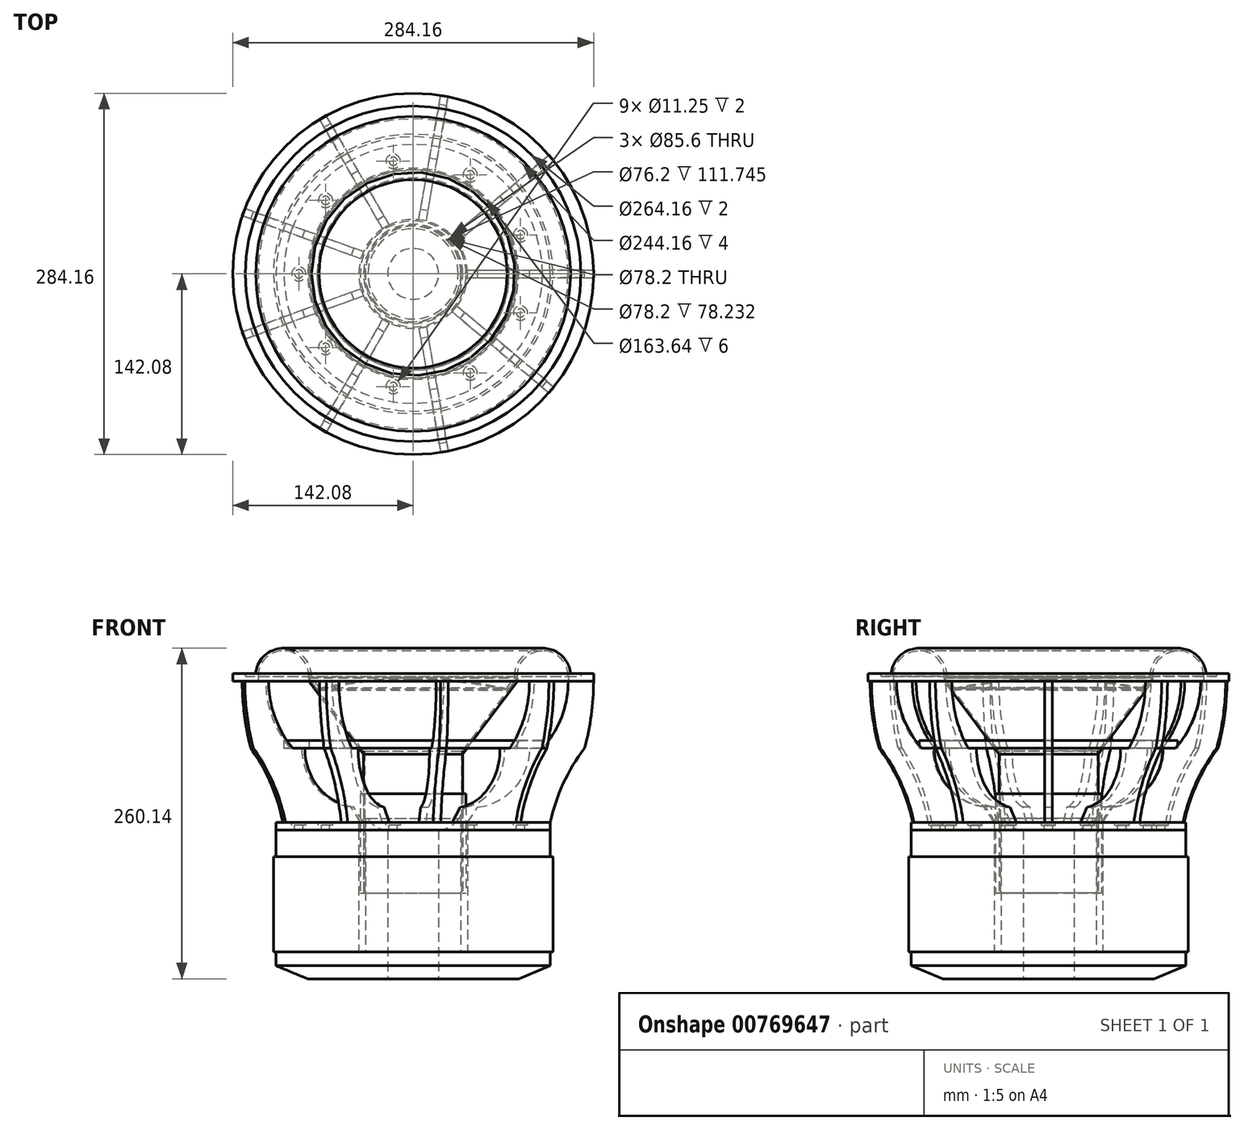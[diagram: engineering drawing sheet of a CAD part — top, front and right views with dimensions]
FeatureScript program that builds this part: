
annotation { "Feature Type Name" : "Feature", "Feature Type Description" : "" }
export const myFeature = defineFeature(function(context is Context, id is Id, definition is map)
    precondition{}
    {
        {
            var Q0;
            Q0=qCreatedBy(makeId("Front.planeOp"),FACE);
            var sketch = newSketch(context, id + "F0", { "sketchPlane" : qUnion([Q0])});
            skLineSegment(sketch, "E0.bottom", {"start": v(42.8, 0) * mm, "end": v(108, 0) * mm});
            skLineSegment(sketch, "E0.top", {"start": v(42.8, -6) * mm, "end": v(108, -6) * mm});
            skLineSegment(sketch, "E0.left", {"start": v(42.8, 0) * mm, "end": v(42.8, -6) * mm});
            skLineSegment(sketch, "E1", {"start": v(108, -6) * mm, "end": v(108, 0) * mm});
            skLineSegment(sketch, "E2", {"start": v(0, 0) * mm, "end": v(0, 32.36) * mm, "construction": true});
            skLineSegment(sketch, "E3.bottom", {"start": v(132.08, 117.12) * mm, "end": v(142.08, 117.12) * mm});
            skLineSegment(sketch, "E3.top", {"start": v(122.08, 111.12) * mm, "end": v(142.08, 111.12) * mm});
            skLineSegment(sketch, "E3.left", {"start": v(122.08, 115.12) * mm, "end": v(122.08, 111.12) * mm});
            skLineSegment(sketch, "E3.right", {"start": v(142.08, 117.12) * mm, "end": v(142.08, 111.12) * mm});
            skLineSegment(sketch, "E4", {"start": v(82.08, 111.12) * mm, "end": v(39.1, 53.62) * mm});
            skLineSegment(sketch, "E5", {"start": v(82.08, 113.62) * mm, "end": v(82.08, 111.12) * mm});
            skLineSegment(sketch, "E6", {"start": v(39.1, 56.13) * mm, "end": v(39.1, 53.62) * mm});
            skLineSegment(sketch, "E7.top", {"start": v(38.1, 56.13) * mm, "end": v(39.1, 56.13) * mm});
            skLineSegment(sketch, "E7.right", {"start": v(39.1, -55.62) * mm, "end": v(39.1, 56.13) * mm});
            skLineSegment(sketch, "E8", {"start": v(38.1, 56.13) * mm, "end": v(38.1, -55.62) * mm});
            skLineSegment(sketch, "E9", {"start": v(82.08, 113.62) * mm, "end": v(0, 113.62) * mm, "construction": true});
            skLineSegment(sketch, "E10", {"start": v(82.08, 113.62) * mm, "end": v(39.1, 56.13) * mm});
            skLineSegment(sketch, "E11", {"start": v(122.08, 115.12) * mm, "end": v(132.08, 115.12) * mm});
            skLineSegment(sketch, "E12", {"start": v(132.08, 115.12) * mm, "end": v(132.08, 117.12) * mm});
            skLineSegment(sketch, "E13.right", {"start": v(110, -27) * mm, "end": v(110, -102) * mm});
            skLineSegment(sketch, "E14.top", {"start": v(108, -6) * mm, "end": v(42.8, -6) * mm});
            skLineSegment(sketch, "E14.left", {"start": v(108, -27) * mm, "end": v(108, -6) * mm});
            skLineSegment(sketch, "E14.right", {"start": v(42.8, -27) * mm, "end": v(42.8, -6) * mm});
            skLineSegment(sketch, "E15.top", {"start": v(83.05, -123) * mm, "end": v(20, -123) * mm});
            skLineSegment(sketch, "E15.left", {"start": v(108, -102) * mm, "end": v(108, -112.7) * mm});
            skLineSegment(sketch, "E15.right", {"start": v(20, -102) * mm, "end": v(20, -123) * mm});
            skLineSegment(sketch, "E16", {"start": v(108, -112.7) * mm, "end": v(83.05, -123) * mm});
            skPoint(sketch, "E17", {"position": v(42.8, -16.5) * mm});
            skLineSegment(sketch, "E18", {"start": v(74.06, 106.24) * mm, "end": v(75.67, 105.04) * mm});
            skArc(sketch, "E19", {"start": v(122.08, 115.12) * mm, "mid": v(101.3, 135.13) * mm, "end": v(82.08, 113.62) * mm});
            skLineSegment(sketch, "E20", {"start": v(132.08, 117.12) * mm, "end": v(123.98, 117.12) * mm});
            skLineSegment(sketch, "E21", {"start": v(74.06, 106.24) * mm, "end": v(80.05, 114.25) * mm});
            skArc(sketch, "E22", {"start": v(123.98, 117.12) * mm, "mid": v(100.62, 137.1) * mm, "end": v(80.05, 114.25) * mm});
            skLineSegment(sketch, "E23", {"start": v(123.98, 117.12) * mm, "end": v(121.98, 117.12) * mm, "construction": true});
            skLineSegment(sketch, "E24", {"start": v(91.82, 58.38) * mm, "end": v(91.82, 64.38) * mm});
            skLineSegment(sketch, "E25", {"start": v(81.82, 58.38) * mm, "end": v(42.8, 0) * mm, "construction": true});
            skLineSegment(sketch, "E26", {"start": v(82.08, 111.12) * mm, "end": v(82.08, 69.15) * mm, "construction": true});
            skCircle(sketch, "E27", {"center": v(102.05, 115.12) * mm, "radius": 20.03 * mm, "construction": true});
            skLineSegment(sketch, "E28", {"start": v(122.08, 111.12) * mm, "end": v(82.08, 69.15) * mm, "construction": true});
            skArc(sketch, "E29", {"start": v(134.94, 58.38) * mm, "mid": v(140.29, 84.51) * mm, "end": v(142.08, 111.12) * mm});
            skLineSegment(sketch, "E30.left", {"start": v(81.82, 58.38) * mm, "end": v(81.82, 64.38) * mm});
            skPoint(sketch, "E30.middle", {"position": v(91.82, 61.38) * mm});
            skLineSegment(sketch, "E31", {"start": v(101.82, 58.38) * mm, "end": v(101.82, 64.38) * mm});
            skLineSegment(sketch, "E32", {"start": v(101.82, 64.38) * mm, "end": v(81.82, 64.38) * mm});
            skArc(sketch, "E33", {"start": v(122.08, 111.12) * mm, "mid": v(116.84, 82.87) * mm, "end": v(101.82, 58.38) * mm});
            skPoint(sketch, "E34.endSnap0", {"position": v(75.4, 0) * mm});
            skLineSegment(sketch, "E35", {"start": v(42.8, 0) * mm, "end": v(50.82, 12) * mm});
            skLineSegment(sketch, "E36", {"start": v(50.82, 12) * mm, "end": v(50.82, 0) * mm});
            skArc(sketch, "E37", {"start": v(91.82, 58.38) * mm, "mid": v(80.1, 27.43) * mm, "end": v(50.82, 12) * mm});
            skLineSegment(sketch, "E38", {"start": v(91.82, 58.38) * mm, "end": v(101.82, 58.38) * mm});
            skLineSegment(sketch, "E39", {"start": v(91.82, 58.38) * mm, "end": v(81.82, 58.38) * mm});
            skLineSegment(sketch, "E40", {"start": v(81.82, 64.38) * mm, "end": v(81.82, 110.77) * mm, "construction": true});
            skLineSegment(sketch, "E41", {"start": v(128.03, 117.12) * mm, "end": v(128.03, 123.12) * mm});
            skLineSegment(sketch, "E42", {"start": v(128.03, 123.12) * mm, "end": v(158.03, 123.12) * mm});
            skLineSegment(sketch, "E43", {"start": v(158.03, 123.12) * mm, "end": v(158.03, 117.12) * mm});
            skLineSegment(sketch, "E44", {"start": v(158.03, 117.12) * mm, "end": v(142.08, 117.12) * mm});
            skLineSegment(sketch, "E45", {"start": v(38.1, -55.62) * mm, "end": v(41.66, -55.62) * mm});
            skLineSegment(sketch, "E46", {"start": v(41.66, -55.62) * mm, "end": v(41.66, 22.62) * mm});
            skLineSegment(sketch, "E47", {"start": v(41.66, 22.62) * mm, "end": v(39.1, 22.62) * mm});
            skLineSegment(sketch, "E48", {"start": v(42.8, -27) * mm, "end": v(42.8, -102) * mm});
            skPoint(sketch, "E49", {"position": v(41.66, -16.5) * mm});
            skLineSegment(sketch, "E50", {"start": v(42.8, -27) * mm, "end": v(110, -27) * mm});
            skLineSegment(sketch, "E51", {"start": v(20, -102) * mm, "end": v(110, -102) * mm});
            skLineSegment(sketch, "E52", {"start": v(110, -52.4) * mm, "end": v(42.8, -52.4) * mm});
            skLineSegment(sketch, "E53", {"start": v(110, -76.6) * mm, "end": v(42.8, -76.6) * mm});
            skArc(sketch, "E54", {"start": v(134.94, 58.38) * mm, "mid": v(118.19, 30.7) * mm, "end": v(108, 0) * mm});
            skLineSegment(sketch, "E55", {"start": v(39.1, -55.62) * mm, "end": v(39.1, -102) * mm, "construction": true});
            skLineSegment(sketch, "E56", {"start": v(50.82, 12) * mm, "end": v(50.82, 58.38) * mm, "construction": true});
            skLineSegment(sketch, "E57", {"start": v(20, -102) * mm, "end": v(20, -6) * mm});
            skLineSegment(sketch, "E58", {"start": v(37.5, -102) * mm, "end": v(37.5, 3.38) * mm});
            skArc(sketch, "E59", {"start": v(20, -6) * mm, "mid": v(29.06, -3.47) * mm, "end": v(35.5, 3.38) * mm});
            skLineSegment(sketch, "E60", {"start": v(20, -6) * mm, "end": v(0, -6) * mm, "construction": true});
            skLineSegment(sketch, "E61", {"start": v(35.5, 3.38) * mm, "end": v(37.5, 3.38) * mm});
            skArc(sketch, "E62", {"start": v(75.67, 105.04) * mm, "mid": v(38.08, 111.47) * mm, "end": v(0, 113.62) * mm});
            skArc(sketch, "E63", {"start": v(75.01, 104.17) * mm, "mid": v(37.74, 110.5) * mm, "end": v(0, 112.62) * mm});
            skLineSegment(sketch, "E64", {"start": v(0, 113.62) * mm, "end": v(0, 112.62) * mm});
            skSolve(sketch);
        }
        {
            var Q0;
            Q0=makeQuery(id+"F0.imprint","IMPRINT",FACE,{"disambiguationData":[TD([[makeQuery(id+"F0.imprint","IMPRINT",EDGE,{"derivedFrom":sQuery(id+"F0.wireOp",EDGE,"E0.bottom")}),1.0]])]});
            var Q1;
            Q1=makeQuery(id+"F0.imprint","IMPRINT",FACE,{"disambiguationData":[TD([[makeQuery(id+"F0.imprint","IMPRINT",EDGE,{"derivedFrom":sQuery(id+"F0.wireOp",EDGE,"E3.top")}),-1.0]])]});
            extrude(context, id + "F1", {"entities" : qUnion([Q0, Q1]), "depth" : 3 * mm, "hasSecondDirection" : true, "secondDirectionOppositeDirection" : true, "secondDirectionDepth" : 3 * mm});
        }
        {
            var Q0;
            Q0=makeQuery(id+"F1.opExtrude","SWEPT_BODY",BODY,{"disambiguationData":[OSD([sQuery(id+"F0.wireOp",EDGE,"E0.bottom"),sQuery(id+"F0.wireOp",EDGE,"6c7cb310-9df3-4df2-87a5-b65033ba0822.top"),sQuery(id+"F0.wireOp",EDGE,"nT3Qd54m-n4Mr-KzPj-ubfg-OKSk5NO6LqhC"),sQuery(id+"F0.wireOp",EDGE,"HfDnNz2e-wXp7-ltQI-1r98-O9Q1wdCByFx3"),sQuery(id+"F0.wireOp",EDGE,"b51f060f-5979-43c8-a97c-01c7b52eec3f")])]});
            var Q1;
            Q1=makeQuery(id+"F1.opExtrude","SWEPT_BODY",BODY,{"disambiguationData":[OSD([sQuery(id+"F0.wireOp",EDGE,"56108468-e6ef-4c31-aa1b-a381e27727b4.top"),sQuery(id+"F0.wireOp",EDGE,"E3.top"),sQuery(id+"F0.wireOp",EDGE,"4c3c0eb7-8127-4a6f-916d-201b3557d1e0"),sQuery(id+"F0.wireOp",EDGE,"e00a4080-055f-4dc8-8bab-c810e85ee1ca"),sQuery(id+"F0.wireOp",EDGE,"936a3c3a-1da7-4d78-9b4e-07095c25ca2c"),sQuery(id+"F0.wireOp",EDGE,"0a553143-d006-4ff2-9b8a-ab2828d84b0a")])]});
            var Q2;
            Q2=sQuery(id+"F0.wireOp",EDGE,"E2");
            circularPattern(context, id + "F2", {"entities" : qUnion([Q0, Q1]), "axis" : qUnion([Q2]), "angle" : 360 * degree, "instanceCount" : 9, "equalSpace" : true});
        }
        {
            var Q0;
            Q0=makeQuery(id+"F0.imprint","IMPRINT",FACE,{"disambiguationData":[TD([[makeQuery(id+"F0.imprint","IMPRINT",EDGE,{"derivedFrom":sQuery(id+"F0.wireOp",EDGE,"E0.bottom")}),-1.0]])]});
            var Q1;
            Q1=makeQuery(id+"F0.imprint","IMPRINT",FACE,{"disambiguationData":[TD([[makeQuery(id+"F0.imprint","IMPRINT",EDGE,{"derivedFrom":sQuery(id+"F0.wireOp",EDGE,"E4")}),-1.0]])]});
            var Q2;
            Q2=makeQuery(id+"F0.imprint","IMPRINT",FACE,{"disambiguationData":[TD([[makeQuery(id+"F0.imprint","IMPRINT",EDGE,{"derivedFrom":sQuery(id+"F0.wireOp",EDGE,"E3.bottom")}),-1.0]])]});
            var Q3;
            {var subQ0=sQuery(id+"F0.wireOp",EDGE,"E24");Q3=makeQuery(id+"F0.imprint","IMPRINT",FACE,{"disambiguationData":[TD([[makeQuery(id+"F0.imprint","IMPRINT",EDGE,{"derivedFrom":subQ0}),-1.0]])]});}
            var Q4;
            {var subQ0=sQuery(id+"F0.wireOp",EDGE,"E24");Q4=makeQuery(id+"F0.imprint","IMPRINT",FACE,{"disambiguationData":[TD([[makeQuery(id+"F0.imprint","IMPRINT",EDGE,{"derivedFrom":subQ0}),1.0]])]});}
            var Q5;
            {var subQ6=sQuery(id+"F0.wireOp",EDGE,"E52");Q5=makeQuery(id+"F0.imprint","IMPRINT",FACE,{"disambiguationData":[TD([[makeQuery(id+"F0.imprint","IMPRINT",EDGE,{"derivedFrom":subQ6}),-1.0]])]});}
            var Q6;
            {var subQ0=sQuery(id+"F0.wireOp",EDGE,"E52");Q6=makeQuery(id+"F0.imprint","IMPRINT",FACE,{"disambiguationData":[TD([[makeQuery(id+"F0.imprint","IMPRINT",EDGE,{"derivedFrom":subQ0}),1.0]])]});}
            var Q7;
            {var subQ6=sQuery(id+"F0.wireOp",EDGE,"E53");Q7=makeQuery(id+"F0.imprint","IMPRINT",FACE,{"disambiguationData":[TD([[makeQuery(id+"F0.imprint","IMPRINT",EDGE,{"derivedFrom":subQ6}),1.0]])]});}
            var Q8;
            {var subQ4=sQuery(id+"F0.wireOp",EDGE,"E46");Q8=makeQuery(id+"F0.imprint","IMPRINT",FACE,{"disambiguationData":[TD([[makeQuery(id+"F0.imprint","IMPRINT",EDGE,{"derivedFrom":subQ4}),1.0]])]});}
            var Q9;
            Q9=sQuery(id+"F0.wireOp",EDGE,"E2");
            revolve(context, id + "F3", {"entities" : qUnion([Q0, Q1, Q2, Q3, Q4, Q5, Q6, Q7, Q8]), "axis" : qUnion([Q9]), "revolveType" : RevolveType.FULL});
        }
        {
            var Q0;
            {var subQ5=sQuery(id+"F0.wireOp",EDGE,"E7.top");Q0=makeQuery(id+"F0.imprint","IMPRINT",FACE,{"disambiguationData":[TD([[makeQuery(id+"F0.imprint","IMPRINT",EDGE,{"derivedFrom":subQ5}),-1.0]])]});}
            var Q1;
            {var subQ3=sQuery(id+"F0.wireOp",EDGE,"E14.left");Q1=makeQuery(id+"F0.imprint","IMPRINT",FACE,{"disambiguationData":[TD([[makeQuery(id+"F0.imprint","IMPRINT",EDGE,{"derivedFrom":subQ3}),1.0]])]});}
            var Q2;
            Q2=makeQuery(id+"F0.imprint","IMPRINT",FACE,{"disambiguationData":[TD([[makeQuery(id+"F0.imprint","IMPRINT",EDGE,{"derivedFrom":sQuery(id+"F0.wireOp",EDGE,"E15.top")}),-1.0]])]});
            var Q3;
            Q3=makeQuery(id+"F0.imprint","IMPRINT",FACE,{"disambiguationData":[TD([[makeQuery(id+"F0.imprint","IMPRINT",EDGE,{"derivedFrom":sQuery(id+"F0.wireOp",EDGE,"E11")}),1.0]])]});
            var Q4;
            {var subQ1=sQuery(id+"F0.wireOp",EDGE,"E57");Q4=makeQuery(id+"F0.imprint","IMPRINT",FACE,{"disambiguationData":[TD([[makeQuery(id+"F0.imprint","IMPRINT",EDGE,{"derivedFrom":subQ1}),-1.0]])]});}
            var Q5;
            {var subQ0=sQuery(id+"F0.wireOp",EDGE,"E62");Q5=makeQuery(id+"F0.imprint","IMPRINT",FACE,{"disambiguationData":[TD([[makeQuery(id+"F0.imprint","IMPRINT",EDGE,{"derivedFrom":subQ0}),1.0]])]});}
            var Q6;
            Q6=sQuery(id+"F0.wireOp",EDGE,"E2");
            revolve(context, id + "F4", {"entities" : qUnion([Q0, Q1, Q2, Q3, Q4, Q5]), "axis" : qUnion([Q6]), "revolveType" : RevolveType.FULL, "surfaceOperationType" : NewSurfaceOperationType.NEW});
        }
        {
            var Q0;
            Q0=makeQuery(id+"F3.opRevolve","SWEPT_FACE",FACE,{"disambiguationData":[OSD([sQuery(id+"F0.wireOp",EDGE,"E0.bottom")])]});
            var sketch = newSketch(context, id + "F5", { "sketchPlane" : qUnion([Q0])});
            skPoint(sketch, "E65", {"position": v(-90, 0) * mm});
            skPoint(sketch, "E66.1.0", {"position": v(-68.94, -57.85) * mm});
            skPoint(sketch, "E66.2.0", {"position": v(-15.63, -88.63) * mm});
            skPoint(sketch, "E66.3.0", {"position": v(45, -77.94) * mm});
            skPoint(sketch, "E66.4.0", {"position": v(84.57, -30.78) * mm});
            skPoint(sketch, "E66.center", {"position": v(0, 0) * mm});
            skPoint(sketch, "E67.0.5.0", {"position": v(84.57, 30.78) * mm});
            skPoint(sketch, "E68.0.6.0", {"position": v(45, 77.94) * mm});
            skPoint(sketch, "E68.0.7.0", {"position": v(-15.63, 88.63) * mm});
            skPoint(sketch, "E68.0.8.0", {"position": v(-68.94, 57.85) * mm});
            skSolve(sketch);
        }
        {
            var Q0;
            Q0=sQuery(id+"F5.wireOp",VERTEX,"E65");
            var Q1;
            Q1=sQuery(id+"F5.wireOp",VERTEX,"E66.4.0");
            var Q2;
            Q2=sQuery(id+"F5.wireOp",VERTEX,"E66.3.0");
            var Q3;
            Q3=sQuery(id+"F5.wireOp",VERTEX,"E66.2.0");
            var Q4;
            Q4=sQuery(id+"F5.wireOp",VERTEX,"E66.1.0");
            var Q5;
            Q5=sQuery(id+"F5.wireOp",VERTEX,"E67.0.5.0");
            var Q6;
            Q6=sQuery(id+"F5.wireOp",VERTEX,"E68.0.7.0");
            var Q7;
            Q7=sQuery(id+"F5.wireOp",VERTEX,"E68.0.8.0");
            var Q8;
            Q8=sQuery(id+"F5.wireOp",VERTEX,"E68.0.6.0");
            var Q9;
            Q9=makeQuery(id+"F3.opRevolve","SWEPT_BODY",BODY,{"disambiguationData":[OSD([sQuery(id+"F0.wireOp",EDGE,"E0.bottom"),sQuery(id+"F0.wireOp",EDGE,"E0.left"),sQuery(id+"F0.wireOp",EDGE,"E1"),sQuery(id+"F0.wireOp",EDGE,"E14.top")])]});
            hole(context, id + "F6", {"style" : HoleStyle.C_BORE, "endStyle" : HoleEndStyle.THROUGH, "holeDiameter" : 6.6 * mm, "cBoreDiameter" : 11.25 * mm, "cBoreDepth" : 2 * mm, "locations" : qUnion([Q0, Q1, Q2, Q3, Q4, Q5, Q6, Q7, Q8]), "scope" : qUnion([Q9]), "tappedDepth" : 12 * mm, "tapClearance" : 3});
        }
    });
